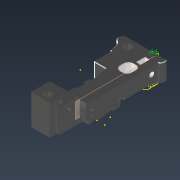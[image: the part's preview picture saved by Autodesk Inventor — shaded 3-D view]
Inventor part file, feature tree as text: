
AUTODESK INVENTOR PART (.ipt)
format: ipt  version: 2022.1 (Build 261234020, 234B)  size: 3,167,744 bytes
history: native  units: mm
features: delete_face x35, extrude x29, sketch x27, reference x22, projected_geometry x19, other x13, chamfer x8, fillet x6, direct_edit x2, move_body x2, hole x1, plane x1
ambient origin geometry x8: Origin, YZ Plane, XZ Plane, XY Plane, X Axis, Y Axis, Z Axis, Center Point
bodies: Volumenkörper1 (feature_tree)
feature tree (165):
  other  "Baugruppe265_right.iam"
  other  "x_carriage_frame_right.ipt:1"
  other  "Bauteil2859.ipt:1"
  extrude  "Extrusion1"  TaperAngle=0.0deg  [1 undecoded]
  delete_face  "Fläche löschen1"
  delete_face  "Fläche löschen2"
  extrude  "Extrusion2"  Depth=10.0mm TaperAngle=0.0deg
  delete_face  "Fläche löschen3"
  delete_face  "Fläche löschen4"
  delete_face  "Fläche löschen5"
  delete_face  "Fläche löschen6"
  delete_face  "Fläche löschen7"
  delete_face  "Fläche löschen8"
  delete_face  "Fläche löschen9"
  delete_face  "Fläche löschen10"
  extrude  "Extrusion3"  Depth=10.0mm TaperAngle=0.0deg
  direct_edit  "Direktbearbeitung1"
  extrude  "Extrusion4"  Depth=10.0mm TaperAngle=0.0deg
  delete_face  "Fläche löschen11"
  delete_face  "Fläche löschen12"
  sketch  "Skizze6"  dims[d16=0.0mm d17=0.0mm d18=1.2mm]
  extrude  "Extrusion5"  Depth=1.2mm
  extrude  "Extrusion6"  TaperAngle=45.0deg  [1 undecoded]
  delete_face  "Fläche löschen13"
  delete_face  "Fläche löschen14"
  extrude  "Extrusion7"  Depth=1.2mm
  delete_face  "Fläche löschen15"
  extrude  "Extrusion8"  Depth=10.0mm TaperAngle=0.0deg
  sketch  "Skizze8"  dims[d21=45.0deg d22=1.2mm]
  delete_face  "Fläche löschen16"
  delete_face  "Fläche löschen17"
  extrude  "Extrusion9"  Depth=16.695228mm
  delete_face  "Fläche löschen18"
  delete_face  "Fläche löschen19"
  delete_face  "Fläche löschen20"
  delete_face  "Fläche löschen21"
  extrude  "Extrusion10"  Depth=0.4mm TaperAngle=0.0deg
  delete_face  "Fläche löschen22"
  delete_face  "Fläche löschen23"
  delete_face  "Fläche löschen24"
  delete_face  "Fläche löschen25"
  extrude  "Extrusion11"  Depth=0.2mm
  fillet  "Rundung1"  Radius=0.2mm
  extrude  "Extrusion12"  Depth=10.0mm TaperAngle=0.0deg
  chamfer  "Fase1"  Distance=0.2mm
  delete_face  "Fläche löschen26"
  delete_face  "Fläche löschen27"
  extrude  "Extrusion13"  Depth=2.0mm
  extrude  "Extrusion14"  Depth=6.8mm TaperAngle=0.0deg
  chamfer  "Fase2"  [1 undecoded]
  chamfer  "Fase3"  Distance=2.0mm Angle=45.0deg
  delete_face  "Fläche löschen28"
  extrude  "Extrusion15"  Depth=2.0mm
  extrude  "Extrusion16"  Depth=4.0mm TaperAngle=0.0deg
  hole  "Bohrung1"  [1 undecoded]
  sketch  "Skizze22"  dims[d49=6.4mm]
  extrude  "Extrusion17"  TaperAngle=0.0deg  [1 undecoded]
  extrude  "Extrusion18"  Depth=2.0mm TaperAngle=45.0deg
  delete_face  "Fläche löschen29"
  chamfer  "Fase4"  Distance=2.0mm Angle=45.0deg
  delete_face  "Fläche löschen30"
  chamfer  "Fase5"  [1 undecoded]
  delete_face  "Fläche löschen31"
  sketch  "Skizze23"  dims[d50=6.4mm d51=0.0mm d52=0.0mm d53=0.8mm d54=2.0mm d55=45.0deg]
  extrude  "Extrusion19"  Depth=5.0mm
  extrude  "Extrusion20"  TaperAngle=0.0deg  [1 undecoded]
  delete_face  "Fläche löschen32"
  fillet  "Rundung2"  [1 undecoded]
  fillet  "Rundung3"  Radius=1.0mm
  extrude  "Extrusion21"  Depth=2.6mm TaperAngle=0.0deg
  chamfer  "Fase6"  Angle=135.0deg  [1 undecoded]
  extrude  "Extrusion22"  Depth=2.6mm TaperAngle=0.0deg
  extrude  "Extrusion23"  Depth=5.0mm TaperAngle=0.0deg
  delete_face  "Fläche löschen33"
  delete_face  "Fläche löschen34"
  extrude  "Extrusion24"  Depth=5.0mm
  delete_face  "Fläche löschen35"
  fillet  "Rundung7"  Radius=3.2mm
  fillet  "Rundung8"  Radius=2.0mm
  chamfer  "Fase7"  Distance=3.0mm
  fillet  "Rundung9"  Radius=1.601mm
  extrude  "Extrusion25"  Depth=2.6mm
  extrude  "Extrusion26"  Depth=2.6mm TaperAngle=0.0deg
  extrude  "Extrusion27"  Depth=2.6mm
  plane  "Arbeitsebene1"
  extrude  "Extrusion28"  Depth=2.6mm TaperAngle=0.0deg
  chamfer  "Fase8"  Distance=1.601mm
  direct_edit  "Direktbearbeitung2"
  extrude  "Extrusion29"  Depth=10.0mm TaperAngle=0.0deg
  sketch  "Skizze1"  dims[d0=10.0mm d1=0.0mm d2=0.0mm]
  sketch  "Skizze2"  dims[d3=10.0mm d4=0.0mm d5=10.0mm d6=0.0mm]
  projected_geometry  "Projizierte Kontur1"
  sketch  "Skizze3"  dims[d7=0.0mm d8=0.0mm d9=-2.0mm d10=10.0mm d11=0.0mm]
  projected_geometry  "Projizierte Kontur2"
  sketch  "Skizze5"  dims[d12=10.0mm d13=0.0mm d14=10.0mm d15=0.0mm]
  reference  "Referenz1"
  reference  "Referenz2"
  projected_geometry  "Projizierte Kontur3"
  reference  "Referenz3"
  reference  "Referenz4"
  projected_geometry  "Projizierte Kontur4"
  sketch  "Skizze7"  dims[d19=1.2mm d20=45.0deg]
  projected_geometry  "Projizierte Kontur5"
  projected_geometry  "Projizierte Kontur6"
  projected_geometry  "Projizierte Kontur7"
  projected_geometry  "Projizierte Kontur8"
  projected_geometry  "Projizierte Kontur9"
  sketch  "Skizze9"  dims[d23=0.4mm d24=10.0mm d25=0.0mm]
  reference  "Referenz5"
  reference  "Referenz6"
  reference  "Referenz7"
  reference  "Referenz8"
  projected_geometry  "Projizierte Kontur10"
  projected_geometry  "Projizierte Kontur11"
  sketch  "Skizze13"  dims[d26=16.695228mm d27=16.695228mm]
  projected_geometry  "Projizierte Kontur18"
  sketch  "Skizze14"  dims[d28=0.8mm d29=0.0mm d30=0.4mm d31=0.0mm]
  reference  "Referenz9"
  sketch  "Skizze15"  dims[d32=0.2mm d33=0.2mm d34=0.2mm]
  projected_geometry  "Projizierte Kontur19"
  sketch  "Skizze16"  dims[d35=0.2mm d36=10.0mm d37=0.0mm]
  reference  "Referenz10"
  sketch  "Skizze17"  dims[d38=0.4mm d39=0.2mm d40=0.0mm]
  reference  "Referenz11"
  sketch  "Skizze18"  dims[d41=0.4mm d42=2.0mm d43=45.0deg d44=0.2mm]
  projected_geometry  "Projizierte Kontur20"
  sketch  "Skizze19"  dims[d45=0.2mm d46=6.8mm d47=0.0mm]
  projected_geometry  "Projizierte Kontur21"
  sketch  "Skizze20"  dims[d48=4.0mm]
  projected_geometry  "Projizierte Kontur23"
  reference  "Referenz16"
  projected_geometry  "Projizierte Kontur24"
  sketch  "Skizze24"  dims[d56=0.4mm d57=2.0mm d58=45.0deg d59=3.0mm]
  reference  "Referenz17"
  reference  "Referenz18"
  reference  "Referenz19"
  reference  "Referenz20"
  reference  "Referenz21"
  reference  "Referenz22"
  reference  "Referenz23"
  reference  "Referenz24"
  reference  "Referenz25"
  sketch  "Skizze25"  dims[d60=2.01mm d61=4.0mm d62=0.0mm]
  projected_geometry  "Projizierte Kontur25"
  sketch  "Skizze26"  dims[d63=1.01mm d64=0.0mm]
  projected_geometry  "Projizierte Kontur26"
  sketch  "Skizze27"  dims[d65=1.9mm d66=6.0mm d67=4.0mm d68=2.0mm d69=90.0deg d70=5.0mm d71=20.594885mm d75=0.4mm]
  reference  "Referenz26"
  sketch  "Skizze28"  dims[d76=6.108652mm d77=0.0mm d78=0.0mm]
  sketch  "Skizze29"  dims[d79=10.0mm d80=0.0mm d81=0.4mm d82=2.0mm d83=45.0deg d84=0.4mm d85=2.0mm d86=45.0deg d87=0.0mm d88=0.0mm]
  sketch  "Skizze30"  dims[d89=10.0mm d90=0.0mm d91=5.0mm]
  sketch  "Skizze31"  dims[d92=1.0mm d93=0.0mm d94=0.0mm]
  sketch  "Skizze32"  dims[d95=0.4mm d96=2.0mm d97=45.0deg d98=45.0deg d99=1.0mm d100=8.0mm d101=0.0mm d102=135.0deg d103=8.0mm d104=0.0mm d105=5.0mm d106=0.0mm d110=5.0mm d111=3.2mm d112=0.4mm d113=2.0mm d114=45.0deg d115=3.0mm d116=1.601mm d117=1.601mm d118=6.0mm d119=0.0mm d120=1.601mm d121=6.0mm d122=0.0mm d123=1.601mm d124=10.0mm d125=0.0mm d126=-5.0mm d127=5.6mm d128=5.6mm d129=2.6mm d130=0.0mm d131=30.0deg d132=0.4mm d133=2.0mm d134=45.0deg d135=0.0mm d136=0.0mm d137=-3.0mm d138=2.8mm d139=2.8mm d140=3.4mm d141=2.6mm d142=0.0mm]
  move_body  "Verschieben1"
  other  "<userpath>\Desktop\RAMA_SBNG\Klicky\Carriage_NG.iam"
  other  "Carriage_NG.iam"
  other  "X_Left:1"
  other  "D2F_01:1"
  other  "D2F_01_BASE_1"
  other  "<userpath>\Desktop\RAMA_SBNG\ToolheadNEW\MGN12 X Axis.iam"
  other  "MGN12 X Axis.iam"
  other  "XY Joint - Right:1"
  other  "Microswitch Endstop Pod:1"
  other  "KW10 Microswitch (2):2"
  move_body  "Verschieben2"
note: 9 required parameter values undecoded (feature->parameter linkage not recoverable at this tier; creation-order binding heuristic only, values carry confidence <= 0.55)
